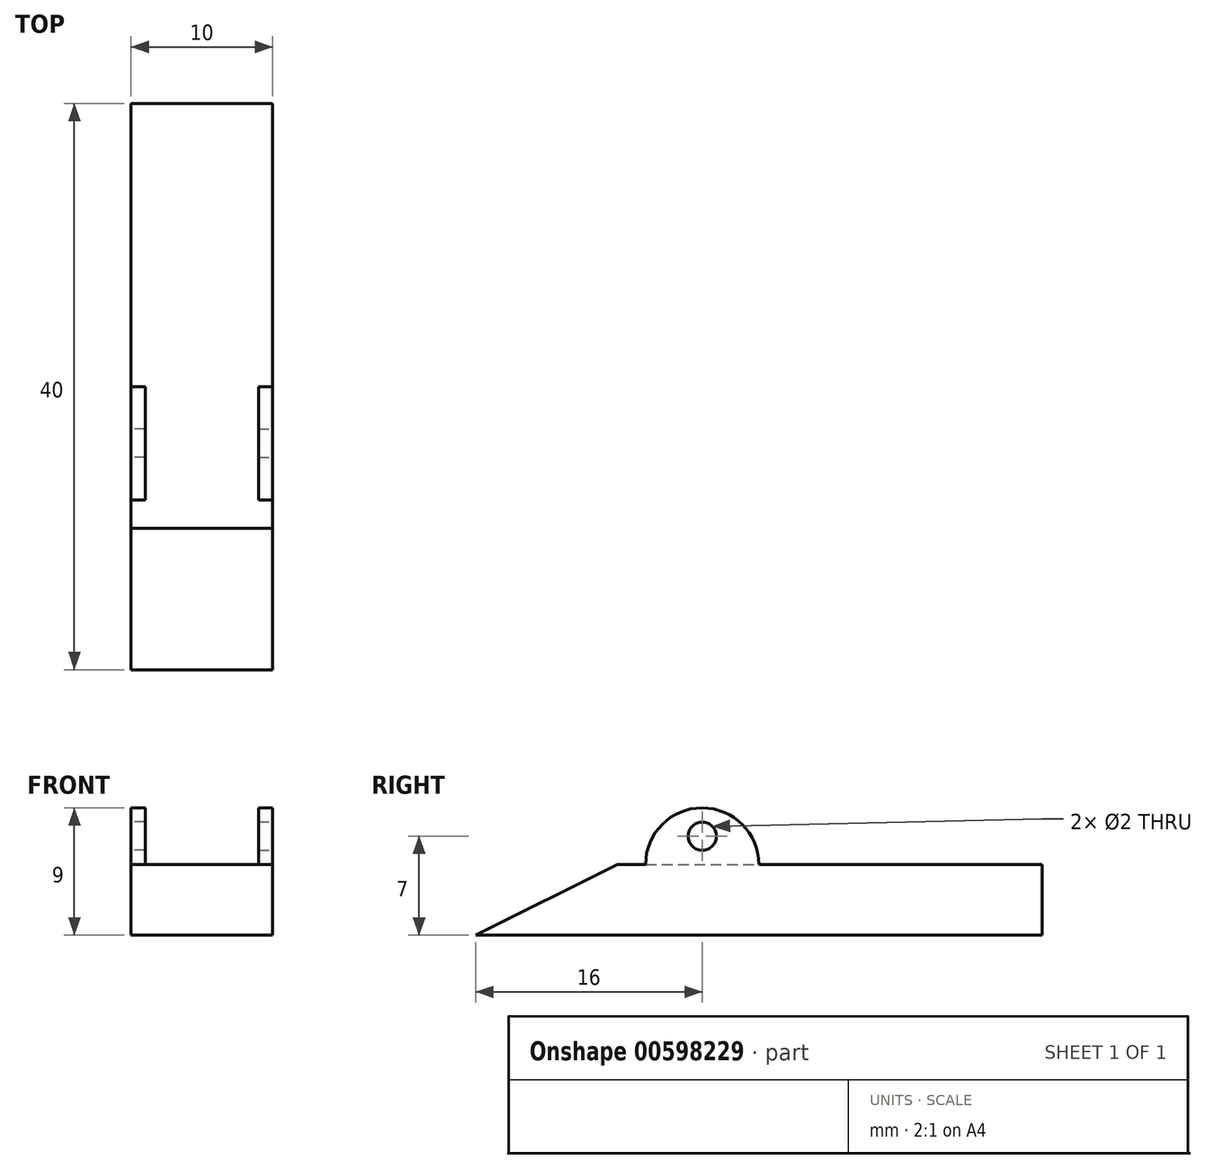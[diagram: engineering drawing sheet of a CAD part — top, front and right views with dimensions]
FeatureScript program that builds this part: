
annotation { "Feature Type Name" : "Feature", "Feature Type Description" : "" }
export const myFeature = defineFeature(function(context is Context, id is Id, definition is map)
    precondition{}
    {
        {
            var Q0;
            Q0=qCreatedBy(makeId("Front.planeOp"),FACE);
            var sketch = newSketch(context, id + "F0", { "sketchPlane" : qUnion([Q0])});
            skLineSegment(sketch, "E0.bottom", {"start": v(-5, -2.5) * mm, "end": v(5, -2.5) * mm});
            skLineSegment(sketch, "E0.top", {"start": v(-5, 2.5) * mm, "end": v(5, 2.5) * mm});
            skLineSegment(sketch, "E0.left", {"start": v(-5, -2.5) * mm, "end": v(-5, 2.5) * mm});
            skLineSegment(sketch, "E0.right", {"start": v(5, -2.5) * mm, "end": v(5, 2.5) * mm});
            skPoint(sketch, "E0.middle", {"position": v(0, 0) * mm});
            skSolve(sketch);
        }
        {
            var Q0;
            Q0=makeQuery(id+"F0.imprint","IMPRINT",FACE,{"disambiguationData":[TD([[makeQuery(id+"F0.imprint","IMPRINT",EDGE,{"derivedFrom":sQuery(id+"F0.wireOp",EDGE,"E0.bottom")}),1.0]])]});
            extrude(context, id + "F1", {"entities" : qUnion([Q0]), "depth" : 40 * mm, "offsetDistance" : 25 * mm});
        }
        {
            var Q0;
            Q0=makeQuery(id+"F1.opExtrude","SWEPT_FACE",FACE,{"disambiguationData":[OSD([sQuery(id+"F0.wireOp",EDGE,"E0.right")])]});
            var sketch = newSketch(context, id + "F2", { "sketchPlane" : qUnion([Q0])});
            skLineSegment(sketch, "E1", {"start": v(-20, 2.5) * mm, "end": v(-24, 2.5) * mm});
            skArc(sketch, "E2", {"start": v(-28, 2.5) * mm, "mid": v(-24, 6.5) * mm, "end": v(-20, 2.5) * mm});
            skCircle(sketch, "E3", {"center": v(-24, 4.5) * mm, "radius": 1 * mm});
            skSolve(sketch);
        }
        {
            var Q0;
            {var subQ0=sQuery(id+"F2.wireOp",EDGE,"E1");Q0=makeQuery(id+"F2.imprint","IMPRINT",FACE,{"disambiguationData":[TD([[makeQuery(id+"F2.imprint","IMPRINT",EDGE,{"derivedFrom":subQ0}),1.0]])]});}
            extrude(context, id + "F3", {"entities" : qUnion([Q0]), "operationType" : NewBodyOperationType.ADD, "oppositeDirection" : true, "depth" : 1 * mm, "offsetDistance" : 25 * mm});
        }
        {
            var Q0;
            Q0=makeQuery(id+"F1.opExtrude","SWEPT_FACE",FACE,{"disambiguationData":[OSD([sQuery(id+"F0.wireOp",EDGE,"E0.left")])]});
            var sketch = newSketch(context, id + "F4", { "sketchPlane" : qUnion([Q0])});
            skLineSegment(sketch, "E4", {"start": v(20, 2.5) * mm, "end": v(28, 2.5) * mm});
            skLineSegment(sketch, "E5", {"start": v(28, 2.5) * mm, "end": v(24, 2.5) * mm});
            skArc(sketch, "E6", {"start": v(20, 2.5) * mm, "mid": v(24, 6.5) * mm, "end": v(28, 2.5) * mm});
            skCircle(sketch, "E7", {"center": v(24, 4.5) * mm, "radius": 1 * mm});
            skSolve(sketch);
        }
        {
            var Q0;
            Q0=makeQuery(id+"F4.imprint","IMPRINT",FACE,{"disambiguationData":[TD([[makeQuery(id+"F4.imprint","IMPRINT",EDGE,{"derivedFrom":sQuery(id+"F4.wireOp",EDGE,"E4")}),-1.0]])]});
            extrude(context, id + "F5", {"entities" : qUnion([Q0]), "operationType" : NewBodyOperationType.ADD, "oppositeDirection" : true, "depth" : 1 * mm, "offsetDistance" : 25 * mm});
        }
        {
            var Q0;
            Q0=makeQuery(id+"F1.opExtrude","CAP_EDGE",EDGE,{"disambiguationData":[OSD([sQuery(id+"F0.wireOp",EDGE,"E0.top")])],"isStart":false});
            chamfer(context, id + "F6", {"entities" : qUnion([Q0]), "chamferType" : ChamferType.TWO_OFFSETS, "width1" : 10 * mm, "oppositeDirection" : false, "width2" : 5 * mm, "tangentPropagation" : true});
        }
    });
